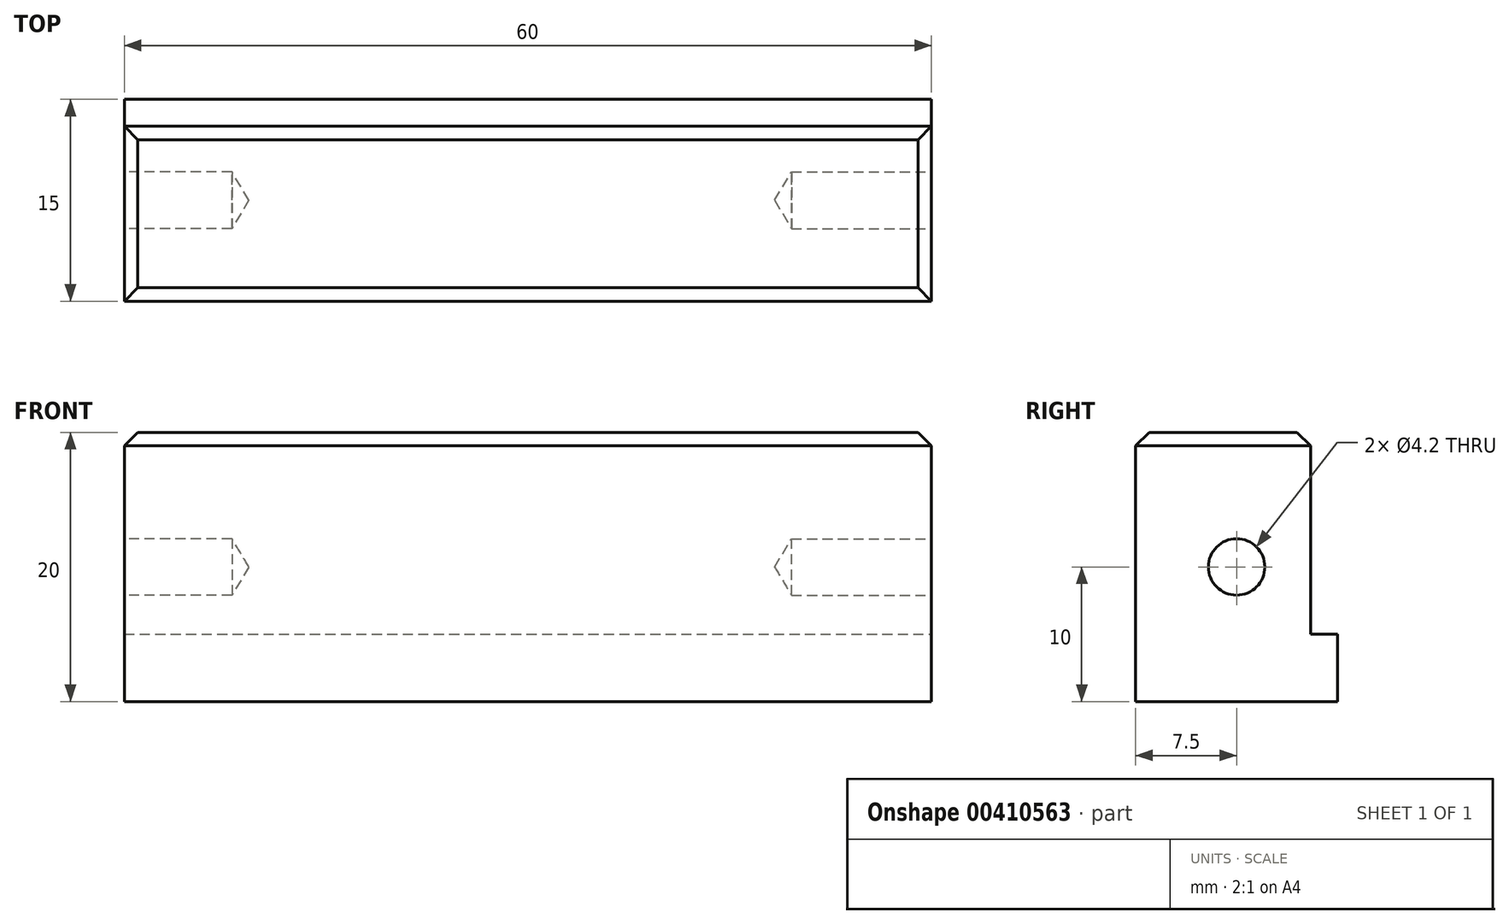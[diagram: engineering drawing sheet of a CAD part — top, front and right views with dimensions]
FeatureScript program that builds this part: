
annotation { "Feature Type Name" : "Feature", "Feature Type Description" : "" }
export const myFeature = defineFeature(function(context is Context, id is Id, definition is map)
    precondition{}
    {
        {
            var Q0;
            Q0=qCreatedBy(makeId("Top.planeOp"),FACE);
            var sketch = newSketch(context, id + "F0", { "sketchPlane" : qUnion([Q0])});
            skLineSegment(sketch, "E0.bottom", {"start": v(0, 0) * mm, "end": v(60, 0) * mm});
            skLineSegment(sketch, "E0.top", {"start": v(0, 15) * mm, "end": v(60, 15) * mm});
            skLineSegment(sketch, "E0.left", {"start": v(0, 0) * mm, "end": v(0, 15) * mm});
            skLineSegment(sketch, "E0.right", {"start": v(60, 0) * mm, "end": v(60, 15) * mm});
            skSolve(sketch);
        }
        {
            var Q0;
            Q0 = qSketchRegion(id + "F0", true);
            extrude(context, id + "F1", {"entities" : qUnion([Q0]), "depth" : 5 * mm});
        }
        {
            var Q0;
            Q0=makeQuery(id+"F1.opExtrude","CAP_FACE",FACE,{"disambiguationData":[OSD([sQuery(id+"F0.wireOp",EDGE,"E0.bottom"),sQuery(id+"F0.wireOp",EDGE,"E0.top"),sQuery(id+"F0.wireOp",EDGE,"E0.left"),sQuery(id+"F0.wireOp",EDGE,"E0.right")])],"isStart":false});
            var sketch = newSketch(context, id + "F2", { "sketchPlane" : qUnion([Q0])});
            skLineSegment(sketch, "E1.bottom", {"start": v(60, 0) * mm, "end": v(0, 0) * mm});
            skLineSegment(sketch, "E1.top", {"start": v(60, 13) * mm, "end": v(0, 13) * mm});
            skLineSegment(sketch, "E1.left", {"start": v(60, 0) * mm, "end": v(60, 13) * mm});
            skLineSegment(sketch, "E1.right", {"start": v(0, 0) * mm, "end": v(0, 13) * mm});
            skSolve(sketch);
        }
        {
            var Q0;
            Q0 = qSketchRegion(id + "F2", true);
            extrude(context, id + "F3", {"entities" : qUnion([Q0]), "operationType" : NewBodyOperationType.ADD, "depth" : 15 * mm});
        }
        {
            var Q0;
            Q0=makeQuery(id+"F3.boolean.opBoolean","MERGE",FACE,{"derivedFrom":[makeQuery(id+"F1.opExtrude","SWEPT_FACE",FACE,{"disambiguationData":[OSD([sQuery(id+"F0.wireOp",EDGE,"E0.right")])]}),makeQuery(id+"F3.opExtrude","SWEPT_FACE",FACE,{"disambiguationData":[OSD([sQuery(id+"F2.wireOp",EDGE,"E1.left")])]})]});
            var sketch = newSketch(context, id + "F4", { "sketchPlane" : qUnion([Q0])});
            skPoint(sketch, "E2", {"position": v(7.5, 10) * mm});
            skSolve(sketch);
        }
        {
            var Q0;
            Q0=sQuery(id+"F4.wireOp",VERTEX,"E2");
            var Q1;
            Q1=makeQuery(id+"F1.opExtrude","SWEPT_BODY",BODY,{"disambiguationData":[OSD([sQuery(id+"F0.wireOp",EDGE,"E0.bottom"),sQuery(id+"F0.wireOp",EDGE,"E0.top"),sQuery(id+"F0.wireOp",EDGE,"E0.left"),sQuery(id+"F0.wireOp",EDGE,"E0.right")])]});
            hole(context, id + "F5", {"style" : HoleStyle.SIMPLE, "endStyle" : HoleEndStyle.BLIND, "standardTappedOrClearance" : lookupTablePath({ "standard" : "ISO", "engagement" : "75%", "pitch" : "0.8 mm", "size" : "M5", "type" : "Tapped" }), "standardBlindInLast" : lookupTablePath({ "standard" : "ISO", "engagement" : "75%", "pitch" : "0.8 mm", "size" : "M5", "type" : "Tapped" }), "holeDiameter" : 4.2 * mm, "showTappedDepth" : true, "holeDepth" : 10.4 * mm, "isTappedThrough" : true, "tappedDepth" : 8 * mm, "tapClearance" : 3, "locations" : qUnion([Q0]), "scope" : qUnion([Q1]), "majorDiameter" : 5 * mm});
        }
        {
            var Q0;
            Q0=makeQuery(id+"F3.boolean.opBoolean","MERGE",FACE,{"derivedFrom":[makeQuery(id+"F1.opExtrude","SWEPT_FACE",FACE,{"disambiguationData":[OSD([sQuery(id+"F0.wireOp",EDGE,"E0.left")])]}),makeQuery(id+"F3.opExtrude","SWEPT_FACE",FACE,{"disambiguationData":[OSD([sQuery(id+"F2.wireOp",EDGE,"E1.right")])]})]});
            var sketch = newSketch(context, id + "F6", { "sketchPlane" : qUnion([Q0])});
            skPoint(sketch, "E3", {"position": v(-7.5, 10) * mm});
            skSolve(sketch);
        }
        {
            var Q0;
            Q0=sQuery(id+"F6.wireOp",VERTEX,"E3");
            var Q1;
            Q1=makeQuery(id+"F1.opExtrude","SWEPT_BODY",BODY,{"disambiguationData":[OSD([sQuery(id+"F0.wireOp",EDGE,"E0.bottom"),sQuery(id+"F0.wireOp",EDGE,"E0.top"),sQuery(id+"F0.wireOp",EDGE,"E0.left"),sQuery(id+"F0.wireOp",EDGE,"E0.right")])]});
            hole(context, id + "F7", {"style" : HoleStyle.SIMPLE, "endStyle" : HoleEndStyle.BLIND, "standardTappedOrClearance" : lookupTablePath({ "standard" : "ISO", "engagement" : "75%", "pitch" : "0.8 mm", "size" : "M5", "type" : "Tapped" }), "standardBlindInLast" : lookupTablePath({ "standard" : "ISO", "engagement" : "75%", "pitch" : "0.8 mm", "size" : "M5", "type" : "Tapped" }), "holeDiameter" : 4.2 * mm, "showTappedDepth" : true, "holeDepth" : 8 * mm, "isTappedThrough" : true, "tappedDepth" : 5.6 * mm, "tapClearance" : 3, "locations" : qUnion([Q0]), "scope" : qUnion([Q1]), "majorDiameter" : 5 * mm});
        }
        {
            var Q0;
            Q0=makeQuery(id+"F3.opExtrude","CAP_EDGE",EDGE,{"disambiguationData":[OSD([sQuery(id+"F2.wireOp",EDGE,"E1.top")])],"isStart":false});
            var Q1;
            Q1=makeQuery(id+"F3.opExtrude","CAP_EDGE",EDGE,{"disambiguationData":[OSD([sQuery(id+"F2.wireOp",EDGE,"E1.bottom")])],"isStart":false});
            var Q2;
            Q2=makeQuery(id+"F3.opExtrude","CAP_EDGE",EDGE,{"disambiguationData":[OSD([sQuery(id+"F2.wireOp",EDGE,"E1.right")])],"isStart":false});
            var Q3;
            Q3=makeQuery(id+"F3.opExtrude","CAP_EDGE",EDGE,{"disambiguationData":[OSD([sQuery(id+"F2.wireOp",EDGE,"E1.left")])],"isStart":false});
            chamfer(context, id + "F8", {"entities" : qUnion([Q0, Q1, Q2, Q3]), "width" : 1 * mm, "tangentPropagation" : true});
        }
    });
